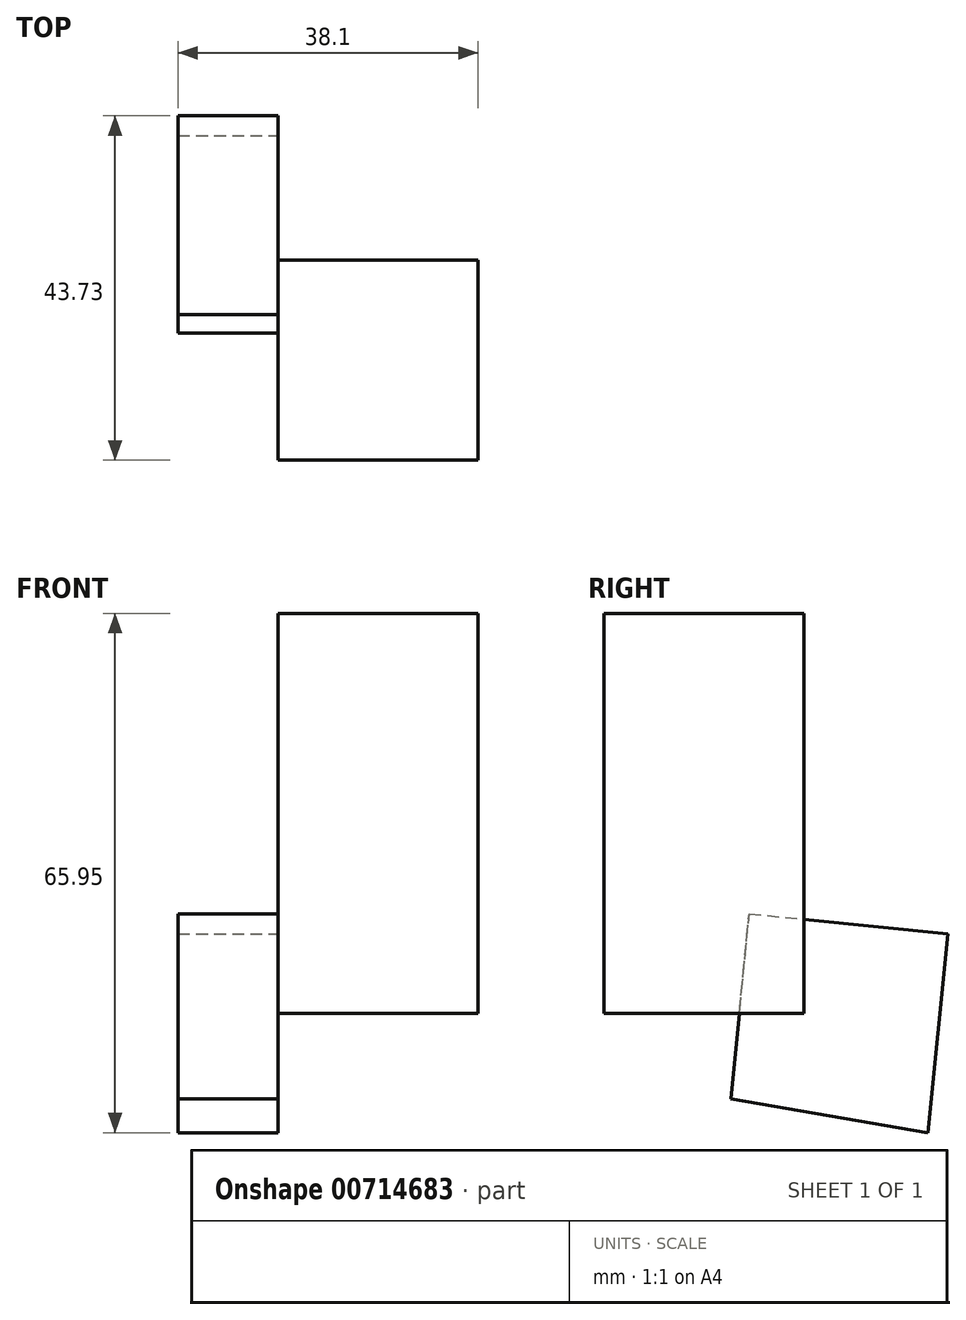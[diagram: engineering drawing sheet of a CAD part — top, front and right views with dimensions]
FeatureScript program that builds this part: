
annotation { "Feature Type Name" : "Feature", "Feature Type Description" : "" }
export const myFeature = defineFeature(function(context is Context, id is Id, definition is map)
    precondition{}
    {
        {
            var Q0;
            Q0=qCreatedBy(makeId("Front.planeOp"),FACE);
            var sketch = newSketch(context, id + "F0", { "sketchPlane" : qUnion([Q0])});
            skLineSegment(sketch, "E0", {"start": v(-26.56, 0) * mm, "end": v(-1.16, 0) * mm});
            skLineSegment(sketch, "E1", {"start": v(-1.16, 0) * mm, "end": v(-1.16, 50.8) * mm});
            skLineSegment(sketch, "E2", {"start": v(-1.16, 50.8) * mm, "end": v(-26.56, 50.8) * mm});
            skLineSegment(sketch, "E3", {"start": v(-26.56, 50.8) * mm, "end": v(-26.56, 0) * mm});
            skSolve(sketch);
        }
        {
            var Q0;
            Q0 = qSketchRegion(id + "F0", true);
            extrude(context, id + "F1", {"entities" : qUnion([Q0]), "depth" : 25.4 * mm, "offsetDistance" : 25.4 * mm});
        }
        {
            var Q0;
            Q0=makeQuery(id+"F1.opExtrude","SWEPT_FACE",FACE,{"disambiguationData":[OSD([sQuery(id+"F0.wireOp",EDGE,"E3")])]});
            var sketch = newSketch(context, id + "F2", { "sketchPlane" : qUnion([Q0])});
            skLineSegment(sketch, "E4", {"start": v(6.95, 12.67) * mm, "end": v(-18.33, 10.12) * mm});
            skLineSegment(sketch, "E5", {"start": v(-18.33, 10.12) * mm, "end": v(-15.78, -15.15) * mm});
            skLineSegment(sketch, "E6", {"start": v(-15.78, -15.15) * mm, "end": v(9.25, -10.88) * mm});
            skLineSegment(sketch, "E7", {"start": v(9.25, -10.88) * mm, "end": v(6.95, 12.67) * mm});
            skSolve(sketch);
        }
        {
            var Q0;
            Q0 = qSketchRegion(id + "F2", true);
            extrude(context, id + "F3", {"entities" : qUnion([Q0]), "operationType" : NewBodyOperationType.ADD, "depth" : 12.7 * mm, "offsetDistance" : 25.4 * mm});
        }
    });
